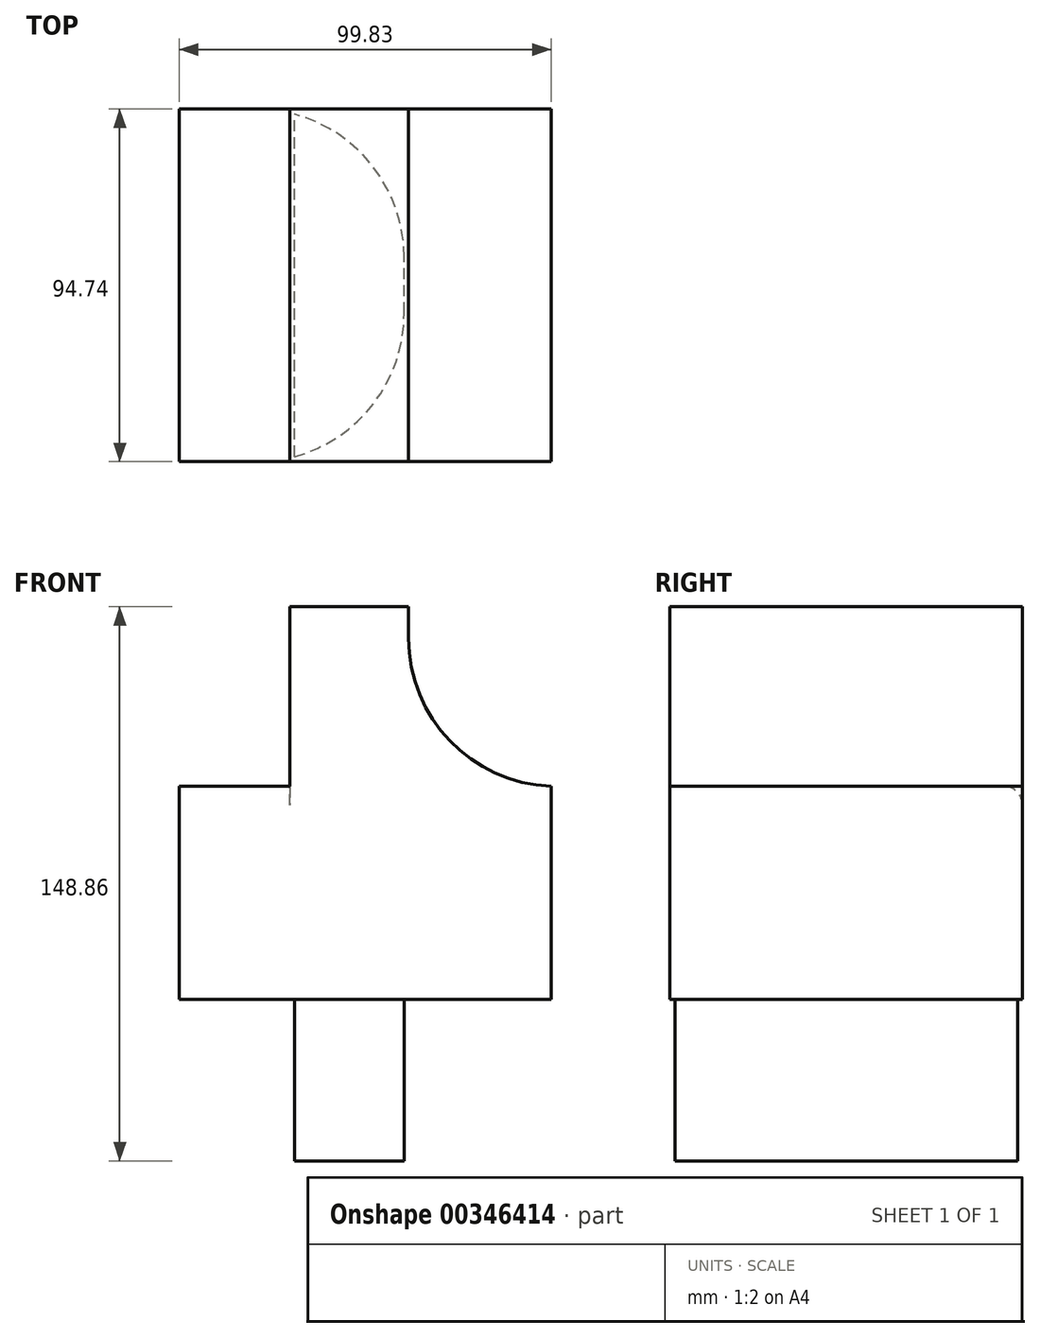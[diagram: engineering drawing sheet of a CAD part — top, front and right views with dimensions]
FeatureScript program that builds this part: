
annotation { "Feature Type Name" : "Feature", "Feature Type Description" : "" }
export const myFeature = defineFeature(function(context is Context, id is Id, definition is map)
    precondition{}
    {
        {
            var Q0;
            Q0=qCreatedBy(makeId("Front.planeOp"),FACE);
            var sketch = newSketch(context, id + "F0", { "sketchPlane" : qUnion([Q0])});
            skLineSegment(sketch, "E0.bottom", {"start": v(-45.63, 31.59) * mm, "end": v(54.2, 31.59) * mm});
            skLineSegment(sketch, "E0.top", {"start": v(-45.63, -25.6) * mm, "end": v(54.2, -25.6) * mm});
            skLineSegment(sketch, "E0.left", {"start": v(-45.63, 31.59) * mm, "end": v(-45.63, -25.6) * mm});
            skLineSegment(sketch, "E0.right", {"start": v(54.2, 31.59) * mm, "end": v(54.2, -25.6) * mm});
            skLineSegment(sketch, "E1.bottom", {"start": v(15.94, 31.59) * mm, "end": v(-15.94, 31.59) * mm});
            skLineSegment(sketch, "E1.top", {"start": v(15.94, 79.81) * mm, "end": v(-15.94, 79.81) * mm});
            skLineSegment(sketch, "E1.left", {"start": v(15.94, 31.59) * mm, "end": v(15.94, 79.81) * mm});
            skLineSegment(sketch, "E1.right", {"start": v(-15.94, 31.59) * mm, "end": v(-15.94, 79.81) * mm});
            skPoint(sketch, "E1.middle", {"position": v(0, 55.7) * mm});
            skLineSegment(sketch, "E2.bottom", {"start": v(-14.75, -25.6) * mm, "end": v(14.75, -25.6) * mm});
            skLineSegment(sketch, "E2.top", {"start": v(-14.75, -69.05) * mm, "end": v(14.75, -69.05) * mm});
            skLineSegment(sketch, "E2.left", {"start": v(-14.75, -25.6) * mm, "end": v(-14.75, -69.05) * mm});
            skLineSegment(sketch, "E2.right", {"start": v(14.75, -25.6) * mm, "end": v(14.75, -69.05) * mm});
            skPoint(sketch, "E2.middle", {"position": v(0, -47.33) * mm});
            skSolve(sketch);
        }
        {
            var Q0;
            Q0 = qSketchRegion(id + "F0", true);
            extrude(context, id + "F1", {"entities" : qUnion([Q0]), "depth" : 94.74 * mm});
        }
        {
            var Q0;
            {var subQ0=sQuery(id+"F0.wireOp",EDGE,"E0.bottom");Q0=makeQuery(id+"F1.opExtrude","CAP_EDGE",EDGE,{"disambiguationData":[OSD([subQ0]),TDD([makeQuery(id+"F0.imprint","IMPRINT",EDGE,{"disambiguationData":[TD([[makeQuery(id+"F0.imprint","INTERSECT",VERTEX,{"derivedFrom":[subQ0,sQuery(id+"F0.wireOp",EDGE,"E0.left")]}),-1.0]])],"derivedFrom":subQ0})])],"isStart":true});}
            fillet(context, id + "F2", {"entities" : qUnion([Q0]), "radius" : 5.08 * mm, "tangentPropagation" : true, "allowEdgeOverflow" : false});
        }
        {
            var Q0;
            Q0=makeQuery(id+"F1.opExtrude","SWEPT_EDGE",EDGE,{"disambiguationData":[OSD([sQuery(id+"F0.wireOp",EDGE,"E0.bottom"),sQuery(id+"F0.wireOp",EDGE,"E1.bottom"),sQuery(id+"F0.wireOp",EDGE,"E1.left")])]});
            var Q1;
            Q1=makeQuery(id+"F1.opExtrude","CAP_EDGE",EDGE,{"disambiguationData":[OSD([sQuery(id+"F0.wireOp",EDGE,"E2.right")])],"isStart":true});
            var Q2;
            Q2=makeQuery(id+"F1.opExtrude","CAP_EDGE",EDGE,{"disambiguationData":[OSD([sQuery(id+"F0.wireOp",EDGE,"E2.right")])],"isStart":false});
            fillet(context, id + "F3", {"entities" : qUnion([Q0, Q1, Q2]), "radius" : 39.86 * mm, "tangentPropagation" : true, "allowEdgeOverflow" : false});
        }
    });
